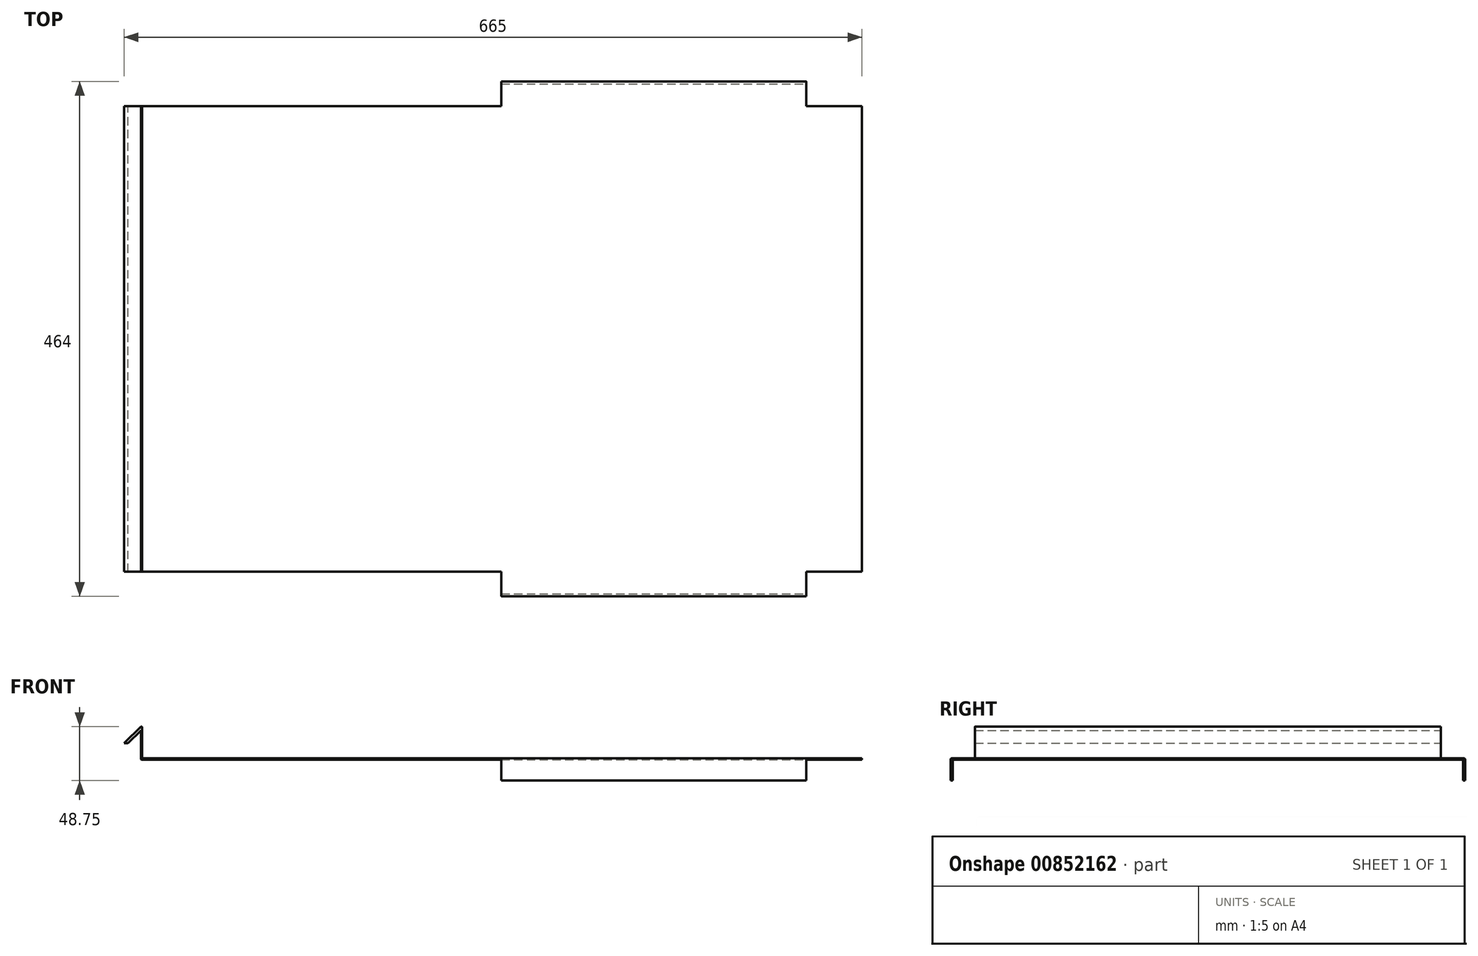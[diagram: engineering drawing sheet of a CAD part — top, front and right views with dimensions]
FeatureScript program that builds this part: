
annotation { "Feature Type Name" : "Feature", "Feature Type Description" : "" }
export const myFeature = defineFeature(function(context is Context, id is Id, definition is map)
    precondition{}
    {
        {
            var Q0;
            Q0=qCreatedBy(makeId("Top.planeOp"),FACE);
            var sketch = newSketch(context, id + "F0", { "sketchPlane" : qUnion([Q0])});
            skLineSegment(sketch, "E0.bottom", {"start": v(275, -232) * mm, "end": v(0, -232) * mm});
            skLineSegment(sketch, "E0.top", {"start": v(275, 232) * mm, "end": v(0, 232) * mm});
            skLineSegment(sketch, "E0.left", {"start": v(325, -210) * mm, "end": v(325, 210) * mm});
            skLineSegment(sketch, "E0.right", {"start": v(-325, -210) * mm, "end": v(-325, 210) * mm});
            skPoint(sketch, "E0.middle", {"position": v(0, 0) * mm});
            skLineSegment(sketch, "E1", {"start": v(-325, -210) * mm, "end": v(0, -210) * mm});
            skLineSegment(sketch, "E2", {"start": v(0, -210) * mm, "end": v(0, -232) * mm});
            skLineSegment(sketch, "E3", {"start": v(275, -232) * mm, "end": v(275, -210) * mm});
            skLineSegment(sketch, "E4", {"start": v(275, -210) * mm, "end": v(325, -210) * mm});
            skPoint(sketch, "E5.orphan", {"position": v(-325, -232) * mm});
            skPoint(sketch, "E6.orphan", {"position": v(325, -232) * mm});
            skLineSegment(sketch, "E7", {"start": v(275, 232) * mm, "end": v(275, 210) * mm});
            skLineSegment(sketch, "E8", {"start": v(0, 210) * mm, "end": v(0, 232) * mm});
            skLineSegment(sketch, "E9", {"start": v(0, 210) * mm, "end": v(-325, 210) * mm});
            skLineSegment(sketch, "E10", {"start": v(275, 210) * mm, "end": v(325, 210) * mm});
            skPoint(sketch, "E11.orphan", {"position": v(-325, 232) * mm});
            skPoint(sketch, "E12.orphan", {"position": v(325, 232) * mm});
            skSolve(sketch);
        }
        {
            var Q0;
            Q0=makeQuery(id+"F0.imprint","IMPRINT",FACE,{"disambiguationData":[TD([[makeQuery(id+"F0.imprint","IMPRINT",EDGE,{"derivedFrom":sQuery(id+"F0.wireOp",EDGE,"E0.bottom")}),-1.0]])]});
            extrude(context, id + "F1", {"entities" : qUnion([Q0]), "depth" : 1.25 * mm, "offsetDistance" : 25 * mm});
        }
        {
            var Q0;
            Q0=makeQuery(id+"F1.opExtrude","CAP_FACE",FACE,{"disambiguationData":[OSD([sQuery(id+"F0.wireOp",EDGE,"E0.bottom"),sQuery(id+"F0.wireOp",EDGE,"E0.top"),sQuery(id+"F0.wireOp",EDGE,"E0.left"),sQuery(id+"F0.wireOp",EDGE,"E0.right"),sQuery(id+"F0.wireOp",EDGE,"E1"),sQuery(id+"F0.wireOp",EDGE,"E2"),sQuery(id+"F0.wireOp",EDGE,"E3"),sQuery(id+"F0.wireOp",EDGE,"E4"),sQuery(id+"F0.wireOp",EDGE,"E7"),sQuery(id+"F0.wireOp",EDGE,"E8"),sQuery(id+"F0.wireOp",EDGE,"E9"),sQuery(id+"F0.wireOp",EDGE,"E10")])],"isStart":false});
            var sketch = newSketch(context, id + "F2", { "sketchPlane" : qUnion([Q0])});
            skLineSegment(sketch, "E13.bottom", {"start": v(0, -232) * mm, "end": v(275, -232) * mm});
            skLineSegment(sketch, "E13.top", {"start": v(0, -230) * mm, "end": v(275, -230) * mm});
            skLineSegment(sketch, "E13.left", {"start": v(0, -232) * mm, "end": v(0, -230) * mm});
            skLineSegment(sketch, "E13.right", {"start": v(275, -232) * mm, "end": v(275, -230) * mm});
            skLineSegment(sketch, "E14.bottom", {"start": v(0, 232) * mm, "end": v(275, 232) * mm});
            skLineSegment(sketch, "E14.top", {"start": v(0, 230) * mm, "end": v(275, 230) * mm});
            skLineSegment(sketch, "E14.left", {"start": v(0, 232) * mm, "end": v(0, 230) * mm});
            skLineSegment(sketch, "E14.right", {"start": v(275, 232) * mm, "end": v(275, 230) * mm});
            skSolve(sketch);
        }
        {
            var Q0;
            Q0=makeQuery(id+"F2.imprint","IMPRINT",FACE,{"disambiguationData":[TD([[makeQuery(id+"F2.imprint","IMPRINT",EDGE,{"derivedFrom":sQuery(id+"F2.wireOp",EDGE,"E14.bottom")}),1.0]])]});
            var Q1;
            Q1=makeQuery(id+"F2.imprint","IMPRINT",FACE,{"disambiguationData":[TD([[makeQuery(id+"F2.imprint","IMPRINT",EDGE,{"derivedFrom":sQuery(id+"F2.wireOp",EDGE,"E13.bottom")}),-1.0]])]});
            extrude(context, id + "F3", {"entities" : qUnion([Q0, Q1]), "operationType" : NewBodyOperationType.ADD, "oppositeDirection" : true, "depth" : 20 * mm, "offsetDistance" : 25 * mm});
        }
        {
            var Q0;
            Q0=makeQuery(id+"F1.opExtrude","CAP_FACE",FACE,{"disambiguationData":[OSD([sQuery(id+"F0.wireOp",EDGE,"E0.bottom"),sQuery(id+"F0.wireOp",EDGE,"E0.top"),sQuery(id+"F0.wireOp",EDGE,"E0.left"),sQuery(id+"F0.wireOp",EDGE,"E0.right"),sQuery(id+"F0.wireOp",EDGE,"E1"),sQuery(id+"F0.wireOp",EDGE,"E2"),sQuery(id+"F0.wireOp",EDGE,"E3"),sQuery(id+"F0.wireOp",EDGE,"E4"),sQuery(id+"F0.wireOp",EDGE,"E7"),sQuery(id+"F0.wireOp",EDGE,"E8"),sQuery(id+"F0.wireOp",EDGE,"E9"),sQuery(id+"F0.wireOp",EDGE,"E10")])],"isStart":true});
            var sketch = newSketch(context, id + "F4", { "sketchPlane" : qUnion([Q0])});
            skLineSegment(sketch, "E15.bottom", {"start": v(-325, 210) * mm, "end": v(-323.75, 210) * mm});
            skLineSegment(sketch, "E15.top", {"start": v(-325, -210) * mm, "end": v(-323.75, -210) * mm});
            skLineSegment(sketch, "E15.left", {"start": v(-325, 210) * mm, "end": v(-325, -210) * mm});
            skLineSegment(sketch, "E15.right", {"start": v(-323.75, 210) * mm, "end": v(-323.75, -210) * mm});
            skSolve(sketch);
        }
        {
            var Q0;
            Q0=makeQuery(id+"F4.imprint","IMPRINT",FACE,{"disambiguationData":[TD([[makeQuery(id+"F4.imprint","IMPRINT",EDGE,{"derivedFrom":sQuery(id+"F4.wireOp",EDGE,"E15.bottom")}),-1.0]])]});
            extrude(context, id + "F5", {"entities" : qUnion([Q0]), "operationType" : NewBodyOperationType.ADD, "oppositeDirection" : true, "depth" : 30 * mm, "offsetDistance" : 25 * mm});
        }
        {
            var Q0;
            Q0=makeQuery(id+"F5.boolean.opBoolean","MERGE",FACE,{"derivedFrom":[makeQuery(id+"F1.opExtrude","SWEPT_FACE",FACE,{"disambiguationData":[OSD([sQuery(id+"F0.wireOp",EDGE,"E0.right")])]}),makeQuery(id+"F5.opExtrude","SWEPT_FACE",FACE,{"disambiguationData":[OSD([sQuery(id+"F4.wireOp",EDGE,"E15.left")])]})]});
            var sketch = newSketch(context, id + "F6", { "sketchPlane" : qUnion([Q0])});
            skLineSegment(sketch, "E16.bottom", {"start": v(-210, 30) * mm, "end": v(210, 30) * mm});
            skLineSegment(sketch, "E16.top", {"start": v(-210, 15) * mm, "end": v(210, 15) * mm});
            skLineSegment(sketch, "E16.left", {"start": v(-210, 30) * mm, "end": v(-210, 15) * mm});
            skLineSegment(sketch, "E16.right", {"start": v(210, 30) * mm, "end": v(210, 15) * mm});
            skSolve(sketch);
        }
        {
            var Q0;
            Q0=makeQuery(id+"F6.imprint","IMPRINT",FACE,{"disambiguationData":[TD([[makeQuery(id+"F6.imprint","IMPRINT",EDGE,{"derivedFrom":sQuery(id+"F6.wireOp",EDGE,"E16.bottom")}),1.0]])]});
            extrude(context, id + "F7", {"entities" : qUnion([Q0]), "operationType" : NewBodyOperationType.ADD, "depth" : 15 * mm, "offsetDistance" : 25 * mm});
        }
        {
            var Q0;
            Q0=makeQuery(id+"F7.opExtrude","CAP_EDGE",EDGE,{"disambiguationData":[OSD([sQuery(id+"F6.wireOp",EDGE,"E16.bottom")])],"isStart":false});
            chamfer(context, id + "F8", {"entities" : qUnion([Q0]), "width" : 15 * mm, "tangentPropagation" : true});
        }
        {
            var Q0;
            Q0=makeQuery(id+"F7.boolean.opBoolean","MERGE",FACE,{"derivedFrom":[makeQuery(id+"F5.boolean.opBoolean","MERGE",FACE,{"derivedFrom":[makeQuery(id+"F1.opExtrude","SWEPT_FACE",FACE,{"disambiguationData":[OSD([sQuery(id+"F0.wireOp",EDGE,"E9")])]}),makeQuery(id+"F5.opExtrude","SWEPT_FACE",FACE,{"disambiguationData":[OSD([sQuery(id+"F4.wireOp",EDGE,"E15.top")])]})]}),makeQuery(id+"F7.opExtrude","SWEPT_FACE",FACE,{"disambiguationData":[OSD([sQuery(id+"F6.wireOp",EDGE,"E16.left")])]})]});
            var sketch = newSketch(context, id + "F9", { "sketchPlane" : qUnion([Q0])});
            skLineSegment(sketch, "E17", {"start": v(325, 26.46) * mm, "end": v(336.46, 15) * mm});
            skLineSegment(sketch, "E18", {"start": v(325, 15) * mm, "end": v(325, 26.46) * mm});
            skSolve(sketch);
        }
        {
            var Q0;
            Q0=makeQuery(id+"F5.opExtrude","CAP_EDGE",EDGE,{"disambiguationData":[OSD([sQuery(id+"F4.wireOp",EDGE,"E15.right")])],"isStart":false});
            fillet(context, id + "F10", {"entities" : qUnion([Q0]), "radius" : 1 * mm, "tangentPropagation" : true, "allowEdgeOverflow" : false});
        }
        {
            var Q0;
            Q0=makeQuery(id+"F1.opExtrude","CAP_EDGE",EDGE,{"disambiguationData":[OSD([sQuery(id+"F0.wireOp",EDGE,"E0.right")])],"isStart":true});
            var Q1;
            Q1=makeQuery(id+"F1.opExtrude","CAP_EDGE",EDGE,{"disambiguationData":[OSD([sQuery(id+"F0.wireOp",EDGE,"E0.top")])],"isStart":false});
            var Q2;
            Q2=makeQuery(id+"F1.opExtrude","CAP_EDGE",EDGE,{"disambiguationData":[OSD([sQuery(id+"F0.wireOp",EDGE,"E0.bottom")])],"isStart":false});
            fillet(context, id + "F11", {"entities" : qUnion([Q0, Q1, Q2]), "radius" : 1 * mm, "tangentPropagation" : true, "allowEdgeOverflow" : false});
        }
        {
            var Q0;
            {var subQ0=sQuery(id+"F9.wireOp",EDGE,"E17");Q0=makeQuery(id+"F9.imprint","IMPRINT",FACE,{"disambiguationData":[TD([[makeQuery(id+"F9.imprint","IMPRINT",EDGE,{"derivedFrom":subQ0}),-1.0]])]});}
            extrude(context, id + "F12", {"entities" : qUnion([Q0]), "operationType" : NewBodyOperationType.REMOVE, "endBound" : BoundingType.THROUGH_ALL, "oppositeDirection" : true, "depth" : 25 * mm, "offsetDistance" : 25 * mm});
        }
    });
